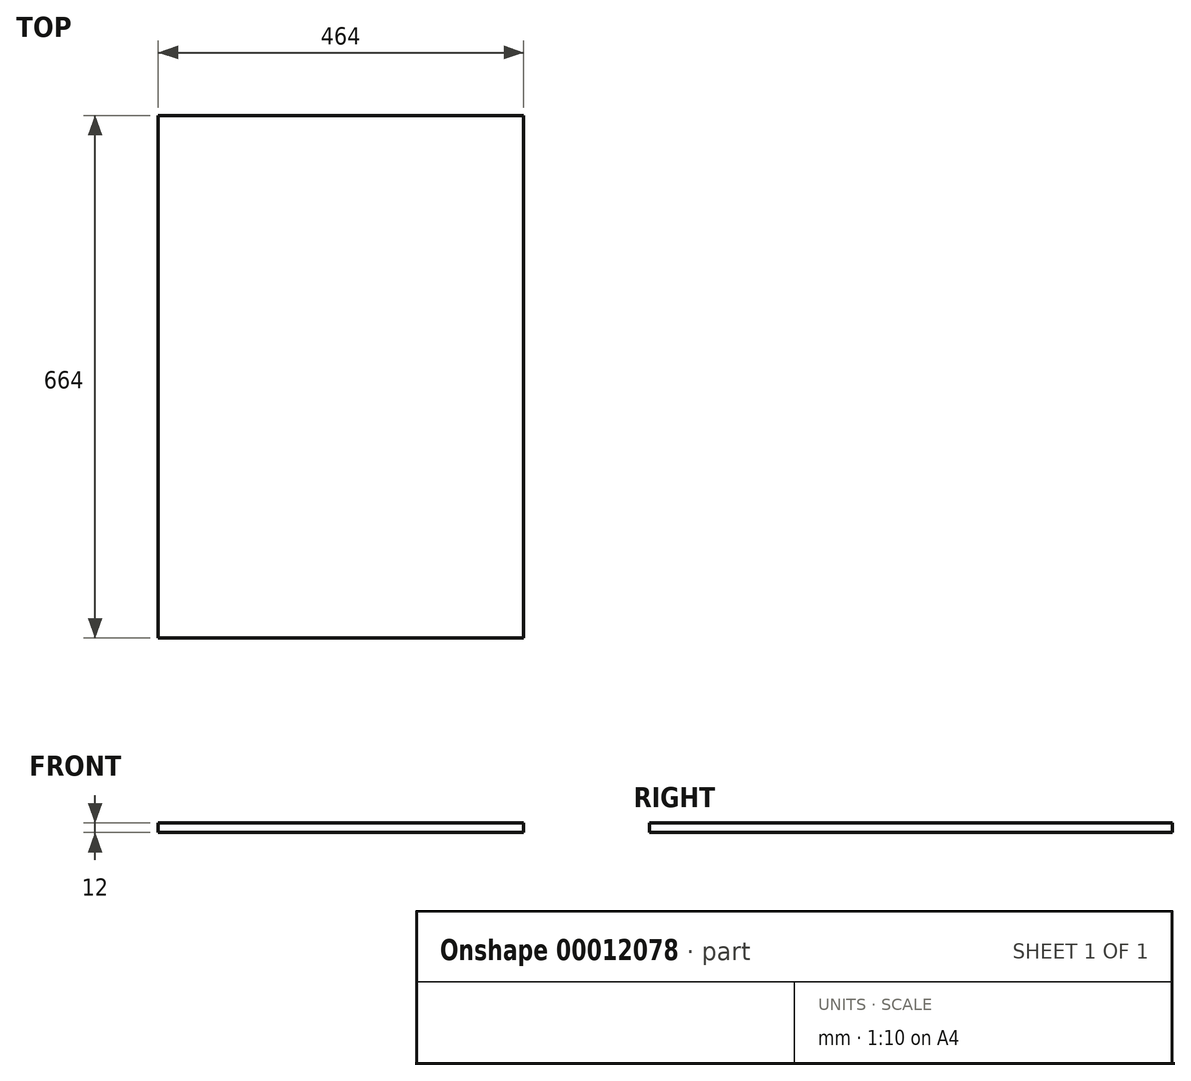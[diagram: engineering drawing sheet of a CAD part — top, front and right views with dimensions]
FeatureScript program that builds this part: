
annotation { "Feature Type Name" : "Feature", "Feature Type Description" : "" }
export const myFeature = defineFeature(function(context is Context, id is Id, definition is map)
    precondition{}
    {
        {
            var Q0;
            Q0=qCreatedBy(makeId("Top.planeOp"),FACE);
            var sketch = newSketch(context, id + "F0", { "sketchPlane" : qUnion([Q0])});
            skLineSegment(sketch, "E0.bottom", {"start": v(0, 0) * mm, "end": v(464, 0) * mm});
            skLineSegment(sketch, "E0.top", {"start": v(0, 664) * mm, "end": v(464, 664) * mm});
            skLineSegment(sketch, "E0.left", {"start": v(0, 0) * mm, "end": v(0, 664) * mm});
            skLineSegment(sketch, "E0.right", {"start": v(464, 0) * mm, "end": v(464, 664) * mm});
            skSolve(sketch);
        }
        {
            var Q0;
            Q0 = qSketchRegion(id + "F0", true);
            extrude(context, id + "F1", {"entities" : qUnion([Q0]), "depth" : 12 * mm});
        }
    });
